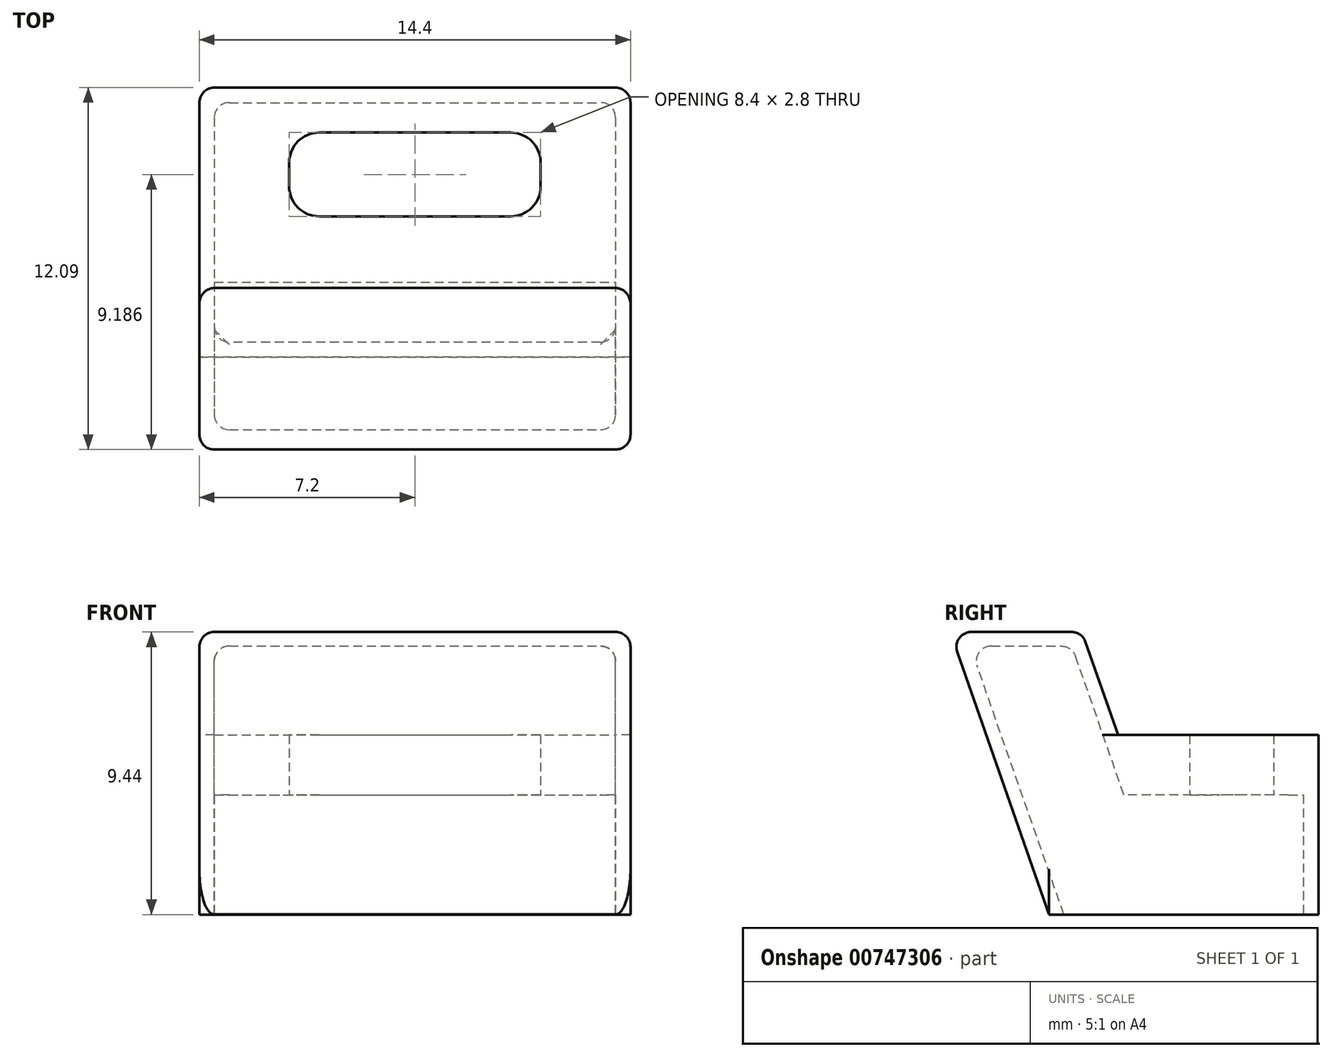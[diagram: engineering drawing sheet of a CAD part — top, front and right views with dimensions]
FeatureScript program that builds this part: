
annotation { "Feature Type Name" : "Feature", "Feature Type Description" : "" }
export const myFeature = defineFeature(function(context is Context, id is Id, definition is map)
    precondition{}
    {
        {
            var Q0;
            Q0=qCreatedBy(makeId("Top.planeOp"),FACE);
            var sketch = newSketch(context, id + "F0", { "sketchPlane" : qUnion([Q0])});
            skLineSegment(sketch, "E0.bottom", {"start": v(0.5, 2.88) * mm, "end": v(13.9, 2.88) * mm});
            skLineSegment(sketch, "E0.top", {"start": v(1.5, 11.88) * mm, "end": v(12.9, 11.88) * mm});
            skLineSegment(sketch, "E0.left", {"start": v(0, 3.38) * mm, "end": v(0, 10.38) * mm});
            skLineSegment(sketch, "E0.right", {"start": v(14.4, 3.38) * mm, "end": v(14.4, 10.38) * mm});
            skPoint(sketch, "E1.visualSharp", {"position": v(0, 11.88) * mm});
            skPoint(sketch, "E2.visualSharp", {"position": v(14.4, 11.88) * mm});
            skPoint(sketch, "E3.visualSharp", {"position": v(14.4, 2.88) * mm});
            skPoint(sketch, "E4.visualSharp", {"position": v(0, 2.88) * mm});
            skLineSegment(sketch, "E5.bottom", {"start": v(4, 10.38) * mm, "end": v(10.4, 10.38) * mm});
            skLineSegment(sketch, "E5.top", {"start": v(4, 7.58) * mm, "end": v(10.4, 7.58) * mm});
            skLineSegment(sketch, "E5.left", {"start": v(3, 9.38) * mm, "end": v(3, 8.58) * mm});
            skLineSegment(sketch, "E5.right", {"start": v(11.4, 9.38) * mm, "end": v(11.4, 8.58) * mm});
            skPoint(sketch, "E6.visualSharp", {"position": v(3, 10.38) * mm});
            skArc(sketch, "E6.filletArc", {"start": v(4, 10.38) * mm, "mid": v(3.3, 10.08) * mm, "end": v(3, 9.38) * mm});
            skPoint(sketch, "E7.visualSharp", {"position": v(3, 7.58) * mm});
            skArc(sketch, "E7.filletArc", {"start": v(3, 8.58) * mm, "mid": v(3.3, 7.87) * mm, "end": v(4, 7.58) * mm});
            skPoint(sketch, "E8.visualSharp", {"position": v(11.4, 10.38) * mm});
            skArc(sketch, "E8.filletArc", {"start": v(11.4, 9.38) * mm, "mid": v(11.1, 10.08) * mm, "end": v(10.4, 10.38) * mm});
            skPoint(sketch, "E9.visualSharp", {"position": v(11.4, 7.58) * mm});
            skArc(sketch, "E9.filletArc", {"start": v(10.4, 7.58) * mm, "mid": v(11.1, 7.87) * mm, "end": v(11.4, 8.58) * mm});
            skLineSegment(sketch, "E10", {"start": v(0, 3.38) * mm, "end": v(14.4, 3.38) * mm});
            skLineSegment(sketch, "E11", {"start": v(14.4, 3.38) * mm, "end": v(14.4, 2.88) * mm});
            skLineSegment(sketch, "E12", {"start": v(13.9, 2.88) * mm, "end": v(14.4, 2.88) * mm});
            skLineSegment(sketch, "E13", {"start": v(0.5, 2.88) * mm, "end": v(0, 2.88) * mm});
            skLineSegment(sketch, "E14", {"start": v(0, 2.88) * mm, "end": v(0, 3.38) * mm});
            skLineSegment(sketch, "E15", {"start": v(0, 10.38) * mm, "end": v(0, 11.88) * mm});
            skLineSegment(sketch, "E16", {"start": v(1.5, 11.88) * mm, "end": v(0, 11.88) * mm});
            skLineSegment(sketch, "E17", {"start": v(12.9, 11.88) * mm, "end": v(14.4, 11.88) * mm});
            skLineSegment(sketch, "E18", {"start": v(14.4, 10.38) * mm, "end": v(14.4, 11.88) * mm});
            skSolve(sketch);
        }
        {
            var Q0;
            Q0=qSketchRegion(id+"F0",true);
            extrude(context, id + "F1", {"entities" : qUnion([Q0]), "depth" : 6 * mm, "offsetDistance" : 25 * mm});
        }
        {
            var Q0;
            Q0=makeQuery(id+"F1.opExtrude","CAP_FACE",FACE,{"disambiguationData":[OSD([sQuery(id+"F0.wireOp",EDGE,"E0.bottom"),sQuery(id+"F0.wireOp",EDGE,"E0.top"),sQuery(id+"F0.wireOp",EDGE,"E0.left"),sQuery(id+"F0.wireOp",EDGE,"E0.right"),sQuery(id+"F0.wireOp",EDGE,"E1.filletArc"),sQuery(id+"F0.wireOp",EDGE,"E2.filletArc"),sQuery(id+"F0.wireOp",EDGE,"E5.bottom"),sQuery(id+"F0.wireOp",EDGE,"E5.top"),sQuery(id+"F0.wireOp",EDGE,"E5.left"),sQuery(id+"F0.wireOp",EDGE,"E5.right"),sQuery(id+"F0.wireOp",EDGE,"E6.filletArc"),sQuery(id+"F0.wireOp",EDGE,"E7.filletArc"),sQuery(id+"F0.wireOp",EDGE,"E8.filletArc"),sQuery(id+"F0.wireOp",EDGE,"E9.filletArc"),sQuery(id+"F0.wireOp",EDGE,"E11"),sQuery(id+"F0.wireOp",EDGE,"E12"),sQuery(id+"F0.wireOp",EDGE,"E13"),sQuery(id+"F0.wireOp",EDGE,"E14")])],"isStart":true});
            var sketch = newSketch(context, id + "F2", { "sketchPlane" : qUnion([Q0])});
            skLineSegment(sketch, "E19.bottom", {"start": v(14.4, -7.28) * mm, "end": v(0, -7.28) * mm});
            skLineSegment(sketch, "E19.top", {"start": v(14.4, -2.88) * mm, "end": v(0, -2.88) * mm});
            skLineSegment(sketch, "E19.left", {"start": v(14.4, -7.28) * mm, "end": v(14.4, -2.88) * mm});
            skLineSegment(sketch, "E19.right", {"start": v(0, -7.28) * mm, "end": v(0, -2.88) * mm});
            skSolve(sketch);
        }
        {
            var Q0;
            Q0=makeQuery(id+"F1.opExtrude","SWEPT_FACE",FACE,{"disambiguationData":[OSD([sQuery(id+"F0.wireOp",EDGE,"E0.left")])]});
            var sketch = newSketch(context, id + "F3", { "sketchPlane" : qUnion([Q0])});
            skLineSegment(sketch, "E20", {"start": v(-2.88, 0) * mm, "end": v(0.42, 9.44) * mm});
            skSolve(sketch);
        }
        {
            var Q0;
            Q0 = qSketchRegion(id + "F2", true);
            var Q1;
            Q1 = qConstructionFilter(qBodyType(qCreatedBy(id + "F3" ,EDGE), BodyType.WIRE), ConstructionObject.NO);
            sweep(context, id + "F4", {"operationType" : NewBodyOperationType.ADD, "profiles" : qUnion([Q0]), "path" : qUnion([Q1])});
        }
        {
            var Q0;
            Q0=makeQuery(id+"F1.opExtrude","CAP_FACE",FACE,{"disambiguationData":[OSD([sQuery(id+"F0.wireOp",EDGE,"E0.bottom"),sQuery(id+"F0.wireOp",EDGE,"E0.top"),sQuery(id+"F0.wireOp",EDGE,"E0.left"),sQuery(id+"F0.wireOp",EDGE,"E0.right"),sQuery(id+"F0.wireOp",EDGE,"E1.filletArc"),sQuery(id+"F0.wireOp",EDGE,"E2.filletArc"),sQuery(id+"F0.wireOp",EDGE,"E5.bottom"),sQuery(id+"F0.wireOp",EDGE,"E5.top"),sQuery(id+"F0.wireOp",EDGE,"E5.left"),sQuery(id+"F0.wireOp",EDGE,"E5.right"),sQuery(id+"F0.wireOp",EDGE,"E6.filletArc"),sQuery(id+"F0.wireOp",EDGE,"E7.filletArc"),sQuery(id+"F0.wireOp",EDGE,"E8.filletArc"),sQuery(id+"F0.wireOp",EDGE,"E9.filletArc"),sQuery(id+"F0.wireOp",EDGE,"E11"),sQuery(id+"F0.wireOp",EDGE,"E12"),sQuery(id+"F0.wireOp",EDGE,"E13"),sQuery(id+"F0.wireOp",EDGE,"E14")])],"isStart":true});
            var sketch = newSketch(context, id + "F5", { "sketchPlane" : qUnion([Q0])});
            skLineSegment(sketch, "E21.bottom", {"start": v(13.9, -6.78) * mm, "end": v(0.5, -6.78) * mm});
            skLineSegment(sketch, "E21.top", {"start": v(13.9, -3.38) * mm, "end": v(0.5, -3.38) * mm});
            skLineSegment(sketch, "E21.left", {"start": v(13.9, -6.78) * mm, "end": v(13.9, -3.38) * mm});
            skLineSegment(sketch, "E21.right", {"start": v(0.5, -6.78) * mm, "end": v(0.5, -3.38) * mm});
            skSolve(sketch);
        }
        {
            var Q0;
            Q0=qCreatedBy(makeId("Right.planeOp"),FACE);
            var sketch = newSketch(context, id + "F6", { "sketchPlane" : qUnion([Q0])});
            skLineSegment(sketch, "E22", {"start": v(3.62, 8.97) * mm, "end": v(6.75, 0) * mm});
            skSolve(sketch);
        }
        {
            var Q0;
            Q0 = qSketchRegion(id + "F5", true);
            var Q1;
            Q1 = qConstructionFilter(qBodyType(qCreatedBy(id + "F6" ,EDGE), BodyType.WIRE), ConstructionObject.NO);
            sweep(context, id + "F7", {"operationType" : NewBodyOperationType.REMOVE, "profiles" : qUnion([Q0]), "path" : qUnion([Q1]), "keepProfileOrientation" : true});
        }
        {
            var Q0;
            Q0=qCreatedBy(makeId("Top.planeOp"),FACE);
            var sketch = newSketch(context, id + "F8", { "sketchPlane" : qUnion([Q0])});
            skLineSegment(sketch, "E23.bottom", {"start": v(12.4, 11.38) * mm, "end": v(2, 11.38) * mm});
            skLineSegment(sketch, "E23.top", {"start": v(12.4, 3.38) * mm, "end": v(2, 3.38) * mm});
            skLineSegment(sketch, "E23.left", {"start": v(13.9, 9.88) * mm, "end": v(13.9, 4.88) * mm});
            skLineSegment(sketch, "E23.right", {"start": v(0.5, 9.88) * mm, "end": v(0.5, 4.88) * mm});
            skLineSegment(sketch, "E24.bottom", {"start": v(14.5, 3.38) * mm, "end": v(27, 1.5) * mm});
            skPoint(sketch, "E25.visualSharp", {"position": v(0.5, 11.38) * mm});
            skPoint(sketch, "E26.visualSharp", {"position": v(13.9, 11.38) * mm});
            skPoint(sketch, "E27.visualSharp", {"position": v(13.9, 3.38) * mm});
            skLineSegment(sketch, "E28", {"start": v(0.5, 4.88) * mm, "end": v(0.5, 3.38) * mm});
            skLineSegment(sketch, "E29", {"start": v(0.5, 3.38) * mm, "end": v(2, 3.38) * mm});
            skLineSegment(sketch, "E30", {"start": v(13.9, 4.88) * mm, "end": v(13.9, 3.38) * mm});
            skLineSegment(sketch, "E31", {"start": v(12.4, 3.38) * mm, "end": v(13.9, 3.38) * mm});
            skLineSegment(sketch, "E32", {"start": v(0.5, 9.88) * mm, "end": v(0.5, 11.38) * mm});
            skLineSegment(sketch, "E33", {"start": v(2, 11.38) * mm, "end": v(0.5, 11.38) * mm});
            skLineSegment(sketch, "E34", {"start": v(12.4, 11.38) * mm, "end": v(13.9, 11.38) * mm});
            skLineSegment(sketch, "E35", {"start": v(13.9, 11.38) * mm, "end": v(13.9, 9.88) * mm});
            skSolve(sketch);
        }
        {
            var Q0;
            Q0=qSketchRegion(id+"F8",true);
            extrude(context, id + "F9", {"entities" : qUnion([Q0]), "operationType" : NewBodyOperationType.REMOVE, "depth" : 4 * mm, "offsetDistance" : 25 * mm});
        }
        {
            var Q0;
            Q0=makeQuery(id+"F7.boolean.opBoolean","COPY",FACE,{"derivedFrom":makeQuery(id+"F7.opSweep","CAP_FACE",FACE,{"disambiguationData":[OSD([sQuery(id+"F5.wireOp",EDGE,"E21.bottom"),sQuery(id+"F5.wireOp",EDGE,"E21.top"),sQuery(id+"F5.wireOp",EDGE,"E21.left"),sQuery(id+"F5.wireOp",EDGE,"E21.right"),sQuery(id+"F6.wireOp",VERTEX,"E22.end")])],"isStart":false})});
            var Q1;
            Q1=makeQuery(id+"F4.opSweep","CAP_FACE",FACE,{"disambiguationData":[OSD([sQuery(id+"F2.wireOp",EDGE,"E19.bottom"),sQuery(id+"F2.wireOp",EDGE,"E19.top"),sQuery(id+"F2.wireOp",EDGE,"E19.left"),sQuery(id+"F2.wireOp",EDGE,"E19.right"),sQuery(id+"F3.wireOp",VERTEX,"E20.end")])],"isStart":false});
            var Q2;
            Q2=makeQuery(id+"F4.opSweep","SWEPT_EDGE",EDGE,{"disambiguationData":[OSD([sQuery(id+"F0.wireOp",EDGE,"E0.left"),sQuery(id+"F0.wireOp",EDGE,"E14"),sQuery(id+"F0.wireOp",EDGE,"E15"),sQuery(id+"F2.wireOp",EDGE,"E19.bottom"),sQuery(id+"F2.wireOp",EDGE,"E19.right"),sQuery(id+"F3.wireOp",EDGE,"E20")])]});
            var Q3;
            Q3=makeQuery(id+"F4.opSweep","SWEPT_EDGE",EDGE,{"disambiguationData":[OSD([sQuery(id+"F0.wireOp",EDGE,"E0.right"),sQuery(id+"F0.wireOp",EDGE,"E11"),sQuery(id+"F0.wireOp",EDGE,"E18"),sQuery(id+"F2.wireOp",EDGE,"E19.bottom"),sQuery(id+"F2.wireOp",EDGE,"E19.left"),sQuery(id+"F3.wireOp",EDGE,"E20")])]});
            var Q4;
            Q4=makeQuery(id+"F4.opSweep","SWEPT_EDGE",EDGE,{"disambiguationData":[OSD([sQuery(id+"F0.wireOp",EDGE,"E0.left"),sQuery(id+"F0.wireOp",EDGE,"E14"),sQuery(id+"F0.wireOp",EDGE,"E15"),sQuery(id+"F2.wireOp",EDGE,"E19.top"),sQuery(id+"F2.wireOp",EDGE,"E19.right"),sQuery(id+"F3.wireOp",EDGE,"E20")])]});
            var Q5;
            Q5=makeQuery(id+"F4.opSweep","SWEPT_EDGE",EDGE,{"disambiguationData":[OSD([sQuery(id+"F0.wireOp",EDGE,"E0.right"),sQuery(id+"F0.wireOp",EDGE,"E11"),sQuery(id+"F0.wireOp",EDGE,"E18"),sQuery(id+"F2.wireOp",EDGE,"E19.top"),sQuery(id+"F2.wireOp",EDGE,"E19.left"),sQuery(id+"F3.wireOp",EDGE,"E20")])]});
            var Q6;
            Q6=makeQuery(id+"F1.opExtrude","SWEPT_EDGE",EDGE,{"disambiguationData":[OSD([sQuery(id+"F0.wireOp",EDGE,"E17"),sQuery(id+"F0.wireOp",EDGE,"E18")])]});
            var Q7;
            Q7=makeQuery(id+"F1.opExtrude","SWEPT_EDGE",EDGE,{"disambiguationData":[OSD([sQuery(id+"F0.wireOp",EDGE,"E15"),sQuery(id+"F0.wireOp",EDGE,"E16")])]});
            var Q8;
            Q8=makeQuery(id+"F9.boolean.opBoolean","COPY",EDGE,{"derivedFrom":makeQuery(id+"F9.opExtrude","SWEPT_EDGE",EDGE,{"disambiguationData":[OSD([sQuery(id+"F8.wireOp",EDGE,"E32"),sQuery(id+"F8.wireOp",EDGE,"E33")])]})});
            var Q9;
            Q9=makeQuery(id+"F9.boolean.opBoolean","COPY",EDGE,{"derivedFrom":makeQuery(id+"F9.opExtrude","SWEPT_EDGE",EDGE,{"disambiguationData":[OSD([sQuery(id+"F8.wireOp",EDGE,"E34"),sQuery(id+"F8.wireOp",EDGE,"E35")])]})});
            var Q10;
            Q10=makeQuery(id+"F7.boolean.opBoolean","COPY",EDGE,{"derivedFrom":makeQuery(id+"F7.opSweep","SWEPT_EDGE",EDGE,{"disambiguationData":[OSD([sQuery(id+"F5.wireOp",EDGE,"E21.top"),sQuery(id+"F5.wireOp",EDGE,"E21.right"),sQuery(id+"F6.wireOp",EDGE,"E22")])]})});
            var Q11;
            Q11=makeQuery(id+"F7.boolean.opBoolean","COPY",EDGE,{"derivedFrom":makeQuery(id+"F7.opSweep","SWEPT_EDGE",EDGE,{"disambiguationData":[OSD([sQuery(id+"F5.wireOp",EDGE,"E21.top"),sQuery(id+"F5.wireOp",EDGE,"E21.left"),sQuery(id+"F6.wireOp",EDGE,"E22")])]})});
            fillet(context, id + "F10", {"entities" : qUnion([Q0, Q1, Q2, Q3, Q4, Q5, Q6, Q7, Q8, Q9, Q10, Q11]), "radius" : 0.5 * mm, "allowEdgeOverflow" : false});
        }
    });
